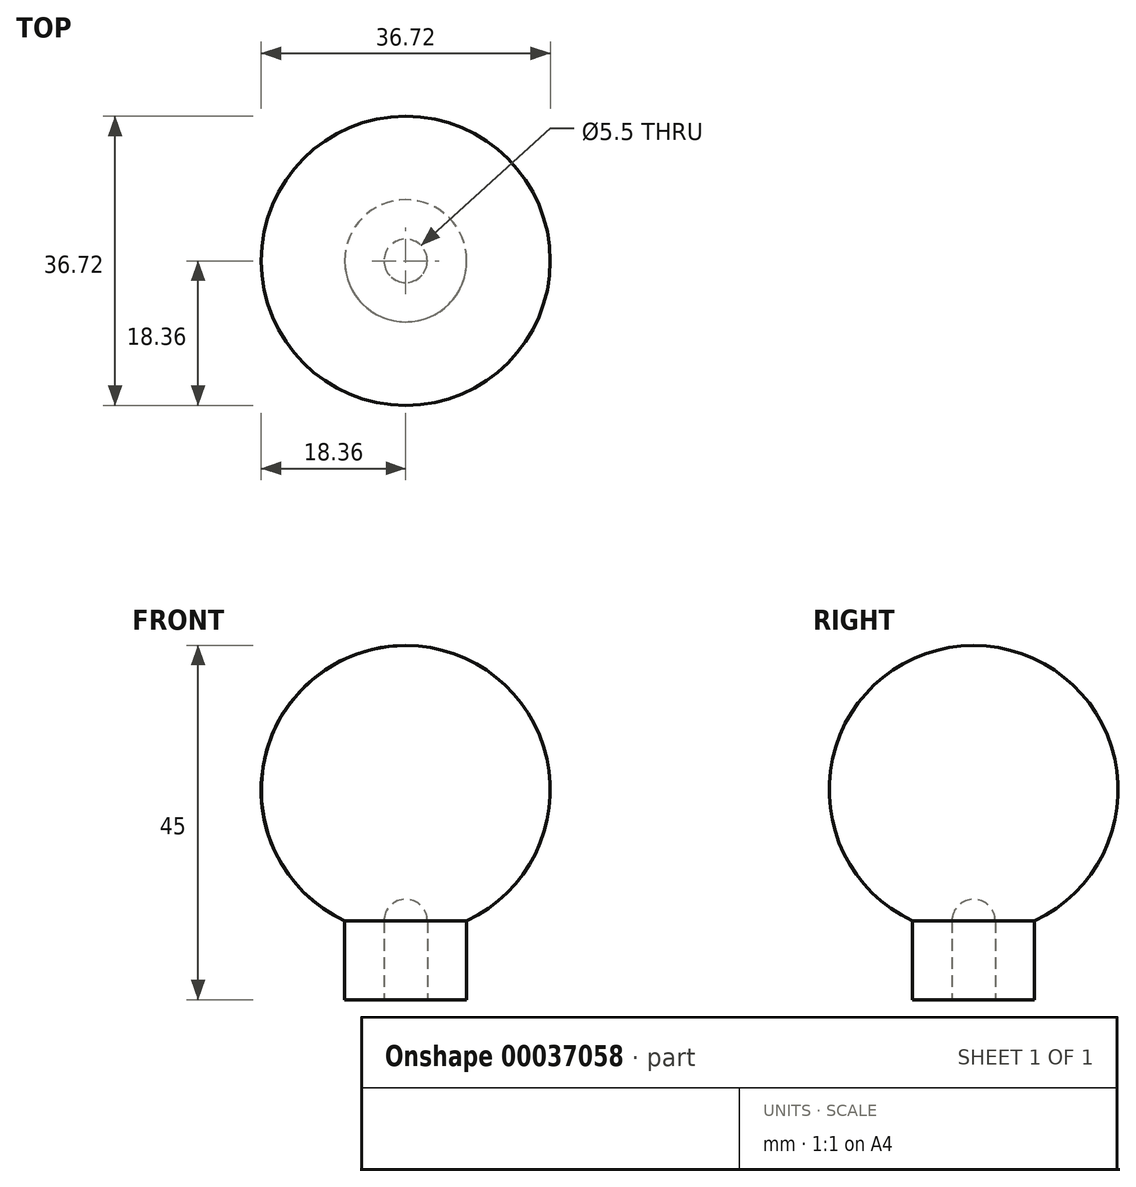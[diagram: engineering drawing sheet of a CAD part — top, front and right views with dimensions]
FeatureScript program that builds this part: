
annotation { "Feature Type Name" : "Feature", "Feature Type Description" : "" }
export const myFeature = defineFeature(function(context is Context, id is Id, definition is map)
    precondition{}
    {
        {
            var Q0;
            Q0=qCreatedBy(makeId("Top.planeOp"),FACE);
            var sketch = newSketch(context, id + "F0", { "sketchPlane" : qUnion([Q0])});
            skCircle(sketch, "E0", {"center": v(0, 0) * mm, "radius": 7.75 * mm});
            skSolve(sketch);
        }
        {
            var Q0;
            Q0 = qSketchRegion(id + "F0", true);
            extrude(context, id + "F1", {"entities" : qUnion([Q0]), "depth" : 10 * mm});
        }
        {
            var Q0;
            Q0=qCreatedBy(makeId("Front.planeOp"),FACE);
            var sketch = newSketch(context, id + "F2", { "sketchPlane" : qUnion([Q0])});
            skLineSegment(sketch, "E1", {"start": v(0, 0) * mm, "end": v(0, 45) * mm, "construction": true});
            skLineSegment(sketch, "E2", {"start": v(0, 45) * mm, "end": v(0, 8.28) * mm});
            skArc(sketch, "E3", {"start": v(0, 8.28) * mm, "mid": v(18.36, 26.64) * mm, "end": v(0, 45) * mm});
            skLineSegment(sketch, "E4.0", {"start": v(-7.75, 10) * mm, "end": v(7.75, 10) * mm, "construction": true});
            skSolve(sketch);
        }
        {
            var Q0;
            Q0=makeQuery(id+"F2.imprint","IMPRINT",FACE,{"disambiguationData":[TD([[makeQuery(id+"F2.imprint","IMPRINT",EDGE,{"derivedFrom":sQuery(id+"F2.wireOp",EDGE,"E2")}),1.0]])]});
            var Q1;
            Q1=sQuery(id+"F2.wireOp",EDGE,"E2");
            revolve(context, id + "F3", {"operationType" : NewBodyOperationType.ADD, "entities" : qUnion([Q0]), "axis" : qUnion([Q1]), "revolveType" : RevolveType.FULL});
        }
        {
            var Q0;
            Q0=makeQuery(id+"F1.opExtrude","CAP_FACE",FACE,{"disambiguationData":[OSD([sQuery(id+"F0.wireOp",EDGE,"E0")])],"isStart":true});
            var sketch = newSketch(context, id + "F4", { "sketchPlane" : qUnion([Q0])});
            skCircle(sketch, "E5", {"center": v(0, 0) * mm, "radius": 2.75 * mm});
            skSolve(sketch);
        }
        {
            var Q0;
            Q0 = qSketchRegion(id + "F4", true);
            extrude(context, id + "F5", {"entities" : qUnion([Q0]), "operationType" : NewBodyOperationType.REMOVE, "oppositeDirection" : true, "depth" : 10 * mm});
        }
        {
            var Q0;
            Q0=qCreatedBy(makeId("Front.planeOp"),FACE);
            var sketch = newSketch(context, id + "F6", { "sketchPlane" : qUnion([Q0])});
            skLineSegment(sketch, "E6.0", {"start": v(-2.75, 10) * mm, "end": v(2.75, 10) * mm});
            skArc(sketch, "E7", {"start": v(2.75, 10) * mm, "mid": v(0, 12.75) * mm, "end": v(-2.75, 10) * mm});
            skSolve(sketch);
        }
        {
            var Q0;
            Q0 = qSketchRegion(id + "F6", true);
            var Q1;
            Q1=sQuery(id+"F6.wireOp",EDGE,"E6.0");
            revolve(context, id + "F7", {"operationType" : NewBodyOperationType.REMOVE, "entities" : qUnion([Q0]), "axis" : qUnion([Q1]), "revolveType" : RevolveType.FULL, "oppositeDirection" : true});
        }
    });
